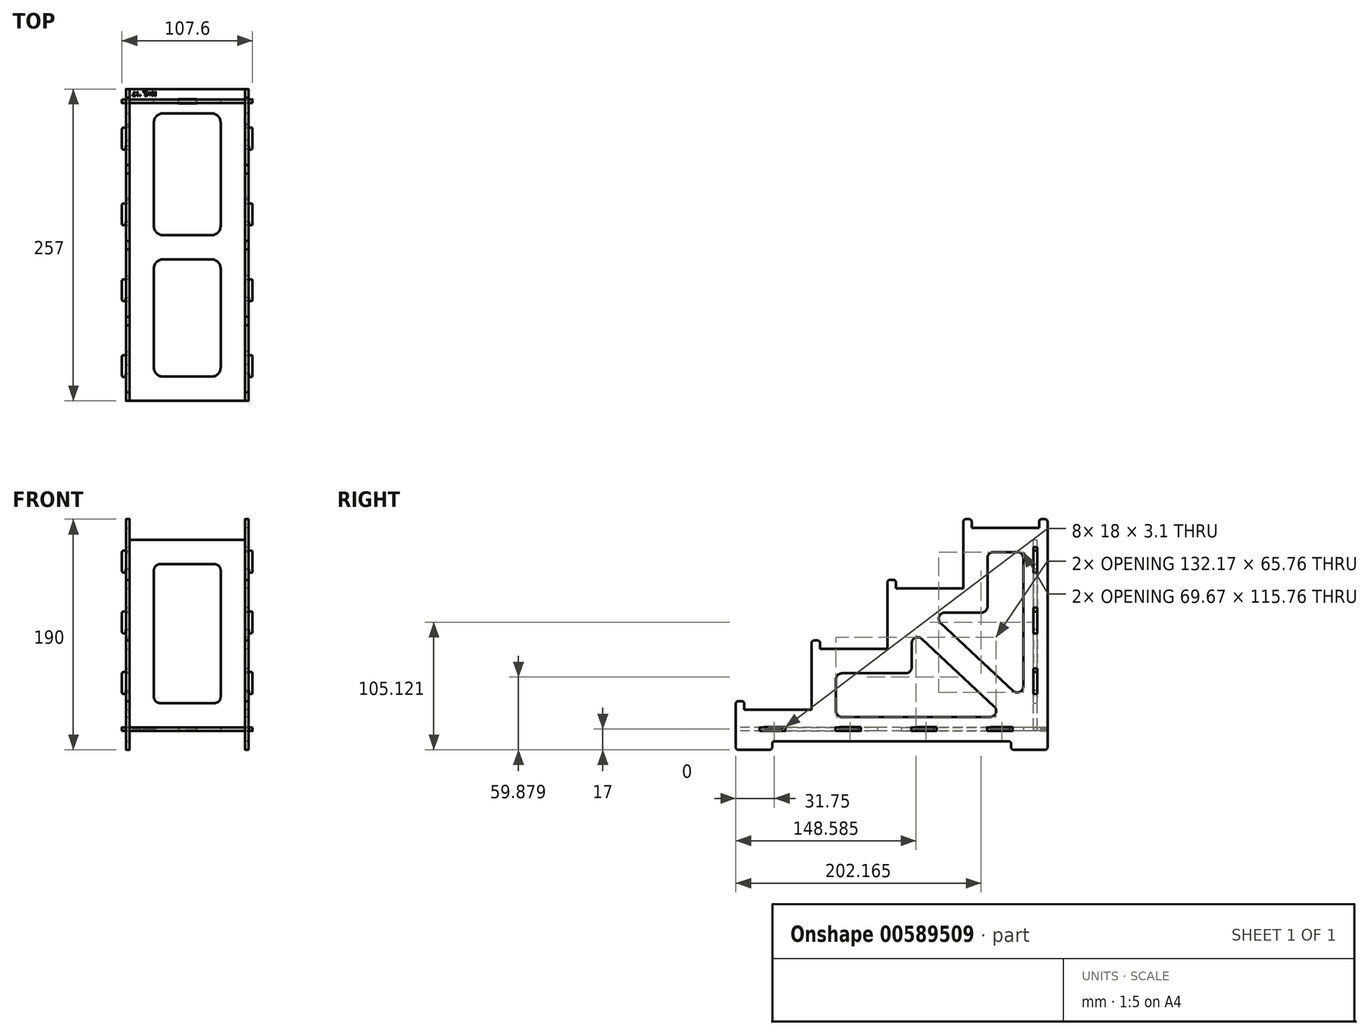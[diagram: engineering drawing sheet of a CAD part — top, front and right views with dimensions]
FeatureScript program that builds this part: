
annotation { "Feature Type Name" : "Feature", "Feature Type Description" : "" }
export const myFeature = defineFeature(function(context is Context, id is Id, definition is map)
    precondition{}
    {
        {
            var Q0;
            Q0=qCreatedBy(makeId("Right.planeOp"),FACE);
            cPlane(context, id + "F0", {"entities" : qUnion([Q0]), "cplaneType" : CPlaneType.OFFSET, "offset" : 95 / 2 * mm, "width" : 150 * mm, "height" : 150 * mm});
        }
        {
            assignVariable(context, id + "F1", {"name" : "Dicke", "anyValue" : 3 * mm});
        }
        {
            var Q0;
            Q0=qCreatedBy(id+"F0.planeOp",FACE);
            var sketch = newSketch(context, id + "F2", { "sketchPlane" : qUnion([Q0])});
            skLineSegment(sketch, "E0", {"start": v(-128.5, 2) * mm, "end": v(-128.5, 38) * mm});
            skLineSegment(sketch, "E1", {"start": v(-126.5, 40) * mm, "end": v(-123.5, 40) * mm});
            skLineSegment(sketch, "E2", {"start": v(-121.5, 38) * mm, "end": v(-121.5, 33) * mm});
            skLineSegment(sketch, "E3", {"start": v(-121.5, 33) * mm, "end": v(-66, 33) * mm});
            skLineSegment(sketch, "E4", {"start": v(-66, 33) * mm, "end": v(-66, 88) * mm});
            skLineSegment(sketch, "E5", {"start": v(-64, 90) * mm, "end": v(-61, 90) * mm});
            skLineSegment(sketch, "E6", {"start": v(-59, 88) * mm, "end": v(-59, 83) * mm});
            skLineSegment(sketch, "E7", {"start": v(-59, 83) * mm, "end": v(-3.5, 83) * mm});
            skLineSegment(sketch, "E8", {"start": v(-3.5, 83) * mm, "end": v(-3.5, 138) * mm});
            skLineSegment(sketch, "E9", {"start": v(-1.5, 140) * mm, "end": v(1.5, 140) * mm});
            skLineSegment(sketch, "E10", {"start": v(3.5, 138) * mm, "end": v(3.5, 133) * mm});
            skLineSegment(sketch, "E11", {"start": v(3.5, 133) * mm, "end": v(59, 133) * mm});
            skLineSegment(sketch, "E12", {"start": v(59, 133) * mm, "end": v(59, 188) * mm});
            skLineSegment(sketch, "E13", {"start": v(61, 190) * mm, "end": v(64, 190) * mm});
            skLineSegment(sketch, "E14", {"start": v(66, 188) * mm, "end": v(66, 183) * mm});
            skLineSegment(sketch, "E15", {"start": v(66, 183) * mm, "end": v(121.5, 183) * mm});
            skLineSegment(sketch, "E16", {"start": v(121.5, 183) * mm, "end": v(121.5, 188) * mm});
            skLineSegment(sketch, "E17", {"start": v(123.5, 190) * mm, "end": v(126.5, 190) * mm});
            skLineSegment(sketch, "E18", {"start": v(128.5, 188) * mm, "end": v(128.5, 2) * mm});
            skLineSegment(sketch, "E19", {"start": v(-126.5, 0) * mm, "end": v(-100.5, 0) * mm});
            skLineSegment(sketch, "E20", {"start": v(-98.5, 2) * mm, "end": v(-98.5, 5) * mm});
            skLineSegment(sketch, "E21", {"start": v(-96.5, 7) * mm, "end": v(96.5, 7) * mm});
            skLineSegment(sketch, "E22", {"start": v(98.5, 5) * mm, "end": v(98.5, 2) * mm});
            skLineSegment(sketch, "E23", {"start": v(100.5, 0) * mm, "end": v(126.5, 0) * mm});
            skPoint(sketch, "E24.visualSharp", {"position": v(-128.5, 0) * mm});
            skArc(sketch, "E24.filletArc", {"start": v(-128.5, 2) * mm, "mid": v(-127.91, 0.59) * mm, "end": v(-126.5, 0) * mm});
            skPoint(sketch, "E25.visualSharp", {"position": v(-128.5, 40) * mm});
            skArc(sketch, "E25.filletArc", {"start": v(-126.5, 40) * mm, "mid": v(-127.91, 39.41) * mm, "end": v(-128.5, 38) * mm});
            skPoint(sketch, "E26.visualSharp", {"position": v(-121.5, 40) * mm});
            skArc(sketch, "E26.filletArc", {"start": v(-121.5, 38) * mm, "mid": v(-122.09, 39.41) * mm, "end": v(-123.5, 40) * mm});
            skPoint(sketch, "E27.visualSharp", {"position": v(-66, 90) * mm});
            skArc(sketch, "E27.filletArc", {"start": v(-64, 90) * mm, "mid": v(-65.41, 89.41) * mm, "end": v(-66, 88) * mm});
            skPoint(sketch, "E28.visualSharp", {"position": v(-59, 90) * mm});
            skArc(sketch, "E28.filletArc", {"start": v(-59, 88) * mm, "mid": v(-59.59, 89.41) * mm, "end": v(-61, 90) * mm});
            skPoint(sketch, "E29.visualSharp", {"position": v(-3.5, 140) * mm});
            skArc(sketch, "E29.filletArc", {"start": v(-1.5, 140) * mm, "mid": v(-2.91, 139.41) * mm, "end": v(-3.5, 138) * mm});
            skPoint(sketch, "E30.visualSharp", {"position": v(3.5, 140) * mm});
            skArc(sketch, "E30.filletArc", {"start": v(3.5, 138) * mm, "mid": v(2.91, 139.41) * mm, "end": v(1.5, 140) * mm});
            skPoint(sketch, "E31.visualSharp", {"position": v(59, 190) * mm});
            skArc(sketch, "E31.filletArc", {"start": v(61, 190) * mm, "mid": v(59.59, 189.41) * mm, "end": v(59, 188) * mm});
            skPoint(sketch, "E32.visualSharp", {"position": v(66, 190) * mm});
            skArc(sketch, "E32.filletArc", {"start": v(66, 188) * mm, "mid": v(65.41, 189.41) * mm, "end": v(64, 190) * mm});
            skPoint(sketch, "E33.visualSharp", {"position": v(121.5, 190) * mm});
            skArc(sketch, "E33.filletArc", {"start": v(123.5, 190) * mm, "mid": v(122.09, 189.41) * mm, "end": v(121.5, 188) * mm});
            skPoint(sketch, "E34.visualSharp", {"position": v(128.5, 190) * mm});
            skArc(sketch, "E34.filletArc", {"start": v(128.5, 188) * mm, "mid": v(127.91, 189.41) * mm, "end": v(126.5, 190) * mm});
            skPoint(sketch, "E35.visualSharp", {"position": v(128.5, 0) * mm});
            skArc(sketch, "E35.filletArc", {"start": v(126.5, 0) * mm, "mid": v(127.91, 0.59) * mm, "end": v(128.5, 2) * mm});
            skPoint(sketch, "E36.visualSharp", {"position": v(98.5, 0) * mm});
            skArc(sketch, "E36.filletArc", {"start": v(98.5, 2) * mm, "mid": v(99.09, 0.59) * mm, "end": v(100.5, 0) * mm});
            skPoint(sketch, "E37.visualSharp", {"position": v(98.5, 7) * mm});
            skArc(sketch, "E37.filletArc", {"start": v(98.5, 5) * mm, "mid": v(97.91, 6.41) * mm, "end": v(96.5, 7) * mm});
            skPoint(sketch, "E38.visualSharp", {"position": v(-98.5, 7) * mm});
            skArc(sketch, "E38.filletArc", {"start": v(-96.5, 7) * mm, "mid": v(-97.91, 6.41) * mm, "end": v(-98.5, 5) * mm});
            skPoint(sketch, "E39.visualSharp", {"position": v(-98.5, 0) * mm});
            skArc(sketch, "E39.filletArc", {"start": v(-100.5, 0) * mm, "mid": v(-99.09, 0.59) * mm, "end": v(-98.5, 2) * mm});
            skLineSegment(sketch, "E40.bottom", {"start": v(-87.75, 15.45) * mm, "end": v(-105.75, 15.45) * mm});
            skLineSegment(sketch, "E40.top", {"start": v(-87.75, 18.55) * mm, "end": v(-105.75, 18.55) * mm});
            skLineSegment(sketch, "E40.left", {"start": v(-87.75, 15.45) * mm, "end": v(-87.75, 18.55) * mm});
            skLineSegment(sketch, "E40.right", {"start": v(-105.75, 15.45) * mm, "end": v(-105.75, 18.55) * mm});
            skPoint(sketch, "E40.middle", {"position": v(-96.75, 17) * mm});
            skPoint(sketch, "E41", {"position": v(-93.75, 33) * mm});
            skPoint(sketch, "E42", {"position": v(-31.25, 83) * mm});
            skPoint(sketch, "E43", {"position": v(31.25, 133) * mm});
            skPoint(sketch, "E44", {"position": v(93.75, 183) * mm});
            skLineSegment(sketch, "E45.1.0.0", {"start": v(-43.25, 15.45) * mm, "end": v(-43.25, 18.55) * mm});
            skLineSegment(sketch, "E45.1.0.1", {"start": v(-25.25, 15.45) * mm, "end": v(-25.25, 18.55) * mm});
            skLineSegment(sketch, "E45.1.0.2", {"start": v(-25.25, 18.55) * mm, "end": v(-43.25, 18.55) * mm});
            skPoint(sketch, "E45.1.0.3", {"position": v(-34.25, 17) * mm});
            skLineSegment(sketch, "E45.1.0.4", {"start": v(-25.25, 15.45) * mm, "end": v(-43.25, 15.45) * mm});
            skLineSegment(sketch, "E45.2.0.0", {"start": v(19.25, 15.45) * mm, "end": v(19.25, 18.55) * mm});
            skLineSegment(sketch, "E45.2.0.1", {"start": v(37.25, 15.45) * mm, "end": v(37.25, 18.55) * mm});
            skLineSegment(sketch, "E45.2.0.2", {"start": v(37.25, 18.55) * mm, "end": v(19.25, 18.55) * mm});
            skPoint(sketch, "E45.2.0.3", {"position": v(28.25, 17) * mm});
            skLineSegment(sketch, "E45.2.0.4", {"start": v(37.25, 15.45) * mm, "end": v(19.25, 15.45) * mm});
            skLineSegment(sketch, "E45.3.0.0", {"start": v(81.75, 15.45) * mm, "end": v(81.75, 18.55) * mm});
            skLineSegment(sketch, "E45.3.0.1", {"start": v(99.75, 15.45) * mm, "end": v(99.75, 18.55) * mm});
            skLineSegment(sketch, "E45.3.0.2", {"start": v(99.75, 18.55) * mm, "end": v(81.75, 18.55) * mm});
            skPoint(sketch, "E45.3.0.3", {"position": v(90.75, 17) * mm});
            skLineSegment(sketch, "E45.3.0.4", {"start": v(99.75, 15.45) * mm, "end": v(81.75, 15.45) * mm});
            skLineSegment(sketch, "E45.direction1", {"start": v(-105.75, 15.45) * mm, "end": v(-43.25, 15.45) * mm, "construction": true});
            skLineSegment(sketch, "E46", {"start": v(-93.75, 33) * mm, "end": v(-93.75, 7) * mm, "construction": true});
            skPoint(sketch, "E47", {"position": v(0, 7) * mm});
            skLineSegment(sketch, "E48.bottom", {"start": v(120.15, 149) * mm, "end": v(116.85, 149) * mm});
            skLineSegment(sketch, "E48.top", {"start": v(120.15, 167) * mm, "end": v(116.85, 167) * mm});
            skLineSegment(sketch, "E48.left", {"start": v(120.15, 149) * mm, "end": v(120.15, 167) * mm});
            skLineSegment(sketch, "E48.right", {"start": v(116.85, 149) * mm, "end": v(116.85, 167) * mm});
            skPoint(sketch, "E48.middle", {"position": v(118.5, 158) * mm});
            skLineSegment(sketch, "E49.1.0.0", {"start": v(120.15, 117) * mm, "end": v(116.85, 117) * mm});
            skLineSegment(sketch, "E49.1.0.1", {"start": v(120.15, 99) * mm, "end": v(116.85, 99) * mm});
            skLineSegment(sketch, "E49.1.0.2", {"start": v(116.85, 99) * mm, "end": v(116.85, 117) * mm});
            skPoint(sketch, "E49.1.0.3", {"position": v(118.5, 108) * mm});
            skLineSegment(sketch, "E49.1.0.4", {"start": v(120.15, 99) * mm, "end": v(120.15, 117) * mm});
            skLineSegment(sketch, "E49.2.0.0", {"start": v(120.15, 67) * mm, "end": v(116.85, 67) * mm});
            skLineSegment(sketch, "E49.2.0.1", {"start": v(120.15, 49) * mm, "end": v(116.85, 49) * mm});
            skLineSegment(sketch, "E49.2.0.2", {"start": v(116.85, 49) * mm, "end": v(116.85, 67) * mm});
            skPoint(sketch, "E49.2.0.3", {"position": v(118.5, 58) * mm});
            skLineSegment(sketch, "E49.2.0.4", {"start": v(120.15, 49) * mm, "end": v(120.15, 67) * mm});
            skLineSegment(sketch, "E49.direction1", {"start": v(116.85, 149) * mm, "end": v(116.85, 99) * mm, "construction": true});
            skLineSegment(sketch, "E50", {"start": v(-46, 32) * mm, "end": v(-46, 58) * mm});
            skLineSegment(sketch, "E51", {"start": v(-41, 63) * mm, "end": v(11.5, 63) * mm});
            skLineSegment(sketch, "E52", {"start": v(16.5, 68) * mm, "end": v(16.5, 87.8) * mm});
            skLineSegment(sketch, "E53", {"start": v(43.81, 113) * mm, "end": v(74, 113) * mm});
            skLineSegment(sketch, "E54", {"start": v(79, 118) * mm, "end": v(79, 158) * mm});
            skLineSegment(sketch, "E55", {"start": v(84, 163) * mm, "end": v(103.5, 163) * mm});
            skLineSegment(sketch, "E56", {"start": v(108.5, 158) * mm, "end": v(108.5, 52.2) * mm});
            skLineSegment(sketch, "E57", {"start": v(81.19, 27) * mm, "end": v(-41, 27) * mm});
            skLineSegment(sketch, "E58", {"start": v(24.91, 91.45) * mm, "end": v(84.6, 35.65) * mm});
            skLineSegment(sketch, "E59", {"start": v(40.4, 104.35) * mm, "end": v(100.09, 48.55) * mm});
            skPoint(sketch, "E60.visualSharp", {"position": v(-46, 27) * mm});
            skArc(sketch, "E60.filletArc", {"start": v(-46, 32) * mm, "mid": v(-44.54, 28.46) * mm, "end": v(-41, 27) * mm});
            skPoint(sketch, "E61.visualSharp", {"position": v(-46, 63) * mm});
            skArc(sketch, "E61.filletArc", {"start": v(-41, 63) * mm, "mid": v(-44.54, 61.54) * mm, "end": v(-46, 58) * mm});
            skPoint(sketch, "E62.visualSharp", {"position": v(16.5, 63) * mm});
            skArc(sketch, "E62.filletArc", {"start": v(11.5, 63) * mm, "mid": v(15.04, 64.46) * mm, "end": v(16.5, 68) * mm});
            skPoint(sketch, "E63.visualSharp", {"position": v(16.5, 99.31) * mm});
            skArc(sketch, "E63.filletArc", {"start": v(24.91, 91.45) * mm, "mid": v(19.5, 92.38) * mm, "end": v(16.5, 87.8) * mm});
            skPoint(sketch, "E64.visualSharp", {"position": v(93.86, 27) * mm});
            skArc(sketch, "E64.filletArc", {"start": v(81.19, 27) * mm, "mid": v(85.84, 30.16) * mm, "end": v(84.6, 35.65) * mm});
            skPoint(sketch, "E65.visualSharp", {"position": v(31.14, 113) * mm});
            skArc(sketch, "E65.filletArc", {"start": v(43.81, 113) * mm, "mid": v(39.16, 109.84) * mm, "end": v(40.4, 104.35) * mm});
            skPoint(sketch, "E66.visualSharp", {"position": v(108.5, 40.69) * mm});
            skArc(sketch, "E66.filletArc", {"start": v(100.09, 48.55) * mm, "mid": v(105.5, 47.62) * mm, "end": v(108.5, 52.2) * mm});
            skPoint(sketch, "E67.visualSharp", {"position": v(79, 113) * mm});
            skArc(sketch, "E67.filletArc", {"start": v(74, 113) * mm, "mid": v(77.54, 114.46) * mm, "end": v(79, 118) * mm});
            skPoint(sketch, "E68.visualSharp", {"position": v(108.5, 163) * mm});
            skArc(sketch, "E68.filletArc", {"start": v(108.5, 158) * mm, "mid": v(107.04, 161.54) * mm, "end": v(103.5, 163) * mm});
            skPoint(sketch, "E69.visualSharp", {"position": v(79, 163) * mm});
            skArc(sketch, "E69.filletArc", {"start": v(84, 163) * mm, "mid": v(80.46, 161.54) * mm, "end": v(79, 158) * mm});
            skSolve(sketch);
        }
        {
            var Q0;
            Q0=makeQuery(id+"F2.imprint","IMPRINT",FACE,{"disambiguationData":[TD([[makeQuery(id+"F2.imprint","IMPRINT",EDGE,{"derivedFrom":sQuery(id+"F2.wireOp",EDGE,"E0")}),-1.0]])]});
            extrude(context, id + "F3", {"entities" : qUnion([Q0]), "depth" : getVariable(context, 'Dicke'), "offsetDistance" : 25 * mm});
        }
        {
            var Q0;
            Q0=makeQuery(id+"F3.opExtrude","SWEPT_BODY",BODY,{"disambiguationData":[OSD([sQuery(id+"F2.wireOp",EDGE,"E0"),sQuery(id+"F2.wireOp",EDGE,"E1"),sQuery(id+"F2.wireOp",EDGE,"E2"),sQuery(id+"F2.wireOp",EDGE,"E3"),sQuery(id+"F2.wireOp",EDGE,"E4"),sQuery(id+"F2.wireOp",EDGE,"E5"),sQuery(id+"F2.wireOp",EDGE,"E6"),sQuery(id+"F2.wireOp",EDGE,"E7"),sQuery(id+"F2.wireOp",EDGE,"E8"),sQuery(id+"F2.wireOp",EDGE,"E9"),sQuery(id+"F2.wireOp",EDGE,"E10"),sQuery(id+"F2.wireOp",EDGE,"E11"),sQuery(id+"F2.wireOp",EDGE,"E12"),sQuery(id+"F2.wireOp",EDGE,"E13"),sQuery(id+"F2.wireOp",EDGE,"E14"),sQuery(id+"F2.wireOp",EDGE,"E15"),sQuery(id+"F2.wireOp",EDGE,"E16"),sQuery(id+"F2.wireOp",EDGE,"E17"),sQuery(id+"F2.wireOp",EDGE,"E18"),sQuery(id+"F2.wireOp",EDGE,"E19"),sQuery(id+"F2.wireOp",EDGE,"E20"),sQuery(id+"F2.wireOp",EDGE,"E21"),sQuery(id+"F2.wireOp",EDGE,"E22"),sQuery(id+"F2.wireOp",EDGE,"E23"),sQuery(id+"F2.wireOp",EDGE,"E24.filletArc"),sQuery(id+"F2.wireOp",EDGE,"E25.filletArc"),sQuery(id+"F2.wireOp",EDGE,"E26.filletArc"),sQuery(id+"F2.wireOp",EDGE,"E27.filletArc"),sQuery(id+"F2.wireOp",EDGE,"E28.filletArc"),sQuery(id+"F2.wireOp",EDGE,"E29.filletArc"),sQuery(id+"F2.wireOp",EDGE,"E30.filletArc"),sQuery(id+"F2.wireOp",EDGE,"E31.filletArc"),sQuery(id+"F2.wireOp",EDGE,"E32.filletArc"),sQuery(id+"F2.wireOp",EDGE,"E33.filletArc"),sQuery(id+"F2.wireOp",EDGE,"E34.filletArc"),sQuery(id+"F2.wireOp",EDGE,"E35.filletArc"),sQuery(id+"F2.wireOp",EDGE,"E36.filletArc"),sQuery(id+"F2.wireOp",EDGE,"E37.filletArc"),sQuery(id+"F2.wireOp",EDGE,"E38.filletArc"),sQuery(id+"F2.wireOp",EDGE,"E39.filletArc")])]});
            var Q1;
            Q1=qCreatedBy(makeId("Right.planeOp"),FACE);
            mirror(context, id + "F4", {"entities" : qUnion([Q0]), "mirrorPlane" : qUnion([Q1])});
        }
        {
            var Q0;
            Q0=qCreatedBy(makeId("Top.planeOp"),FACE);
            var Q1;
            Q1=sQuery(id+"F2.wireOp",VERTEX,"E45.2.0.3");
            cPlane(context, id + "F5", {"entities" : qUnion([Q0, Q1]), "cplaneType" : CPlaneType.PLANE_POINT, "offset" : 25 * mm, "width" : 150 * mm, "height" : 150 * mm});
        }
        {
            var Q0;
            Q0=qCreatedBy(id+"F5.planeOp",FACE);
            var sketch = newSketch(context, id + "F6", { "sketchPlane" : qUnion([Q0])});
            skLineSegment(sketch, "E70", {"start": v(0, 128.5) * mm, "end": v(47.5, 128.5) * mm});
            skLineSegment(sketch, "E71", {"start": v(47.5, 128.5) * mm, "end": v(47.5, 96.75) * mm});
            skLineSegment(sketch, "E72", {"start": v(47.5, 96.75) * mm, "end": v(52.8, 96.75) * mm});
            skLineSegment(sketch, "E73", {"start": v(53.8, 95.75) * mm, "end": v(53.8, 79.75) * mm});
            skLineSegment(sketch, "E74", {"start": v(52.8, 78.75) * mm, "end": v(50.8, 78.75) * mm});
            skLineSegment(sketch, "E75", {"start": v(50.8, 78.75) * mm, "end": v(50.8, 81.75) * mm});
            skLineSegment(sketch, "E76", {"start": v(50.8, 81.75) * mm, "end": v(47.5, 81.75) * mm});
            skLineSegment(sketch, "E77", {"start": v(47.5, 81.75) * mm, "end": v(47.5, 34.25) * mm});
            skLineSegment(sketch, "E78", {"start": v(47.5, 34.25) * mm, "end": v(52.8, 34.25) * mm});
            skLineSegment(sketch, "E79", {"start": v(53.8, 33.25) * mm, "end": v(53.8, 17.25) * mm});
            skLineSegment(sketch, "E80", {"start": v(52.8, 16.25) * mm, "end": v(50.8, 16.25) * mm});
            skLineSegment(sketch, "E81", {"start": v(50.8, 16.25) * mm, "end": v(50.8, 19.25) * mm});
            skLineSegment(sketch, "E82", {"start": v(50.8, 19.25) * mm, "end": v(47.5, 19.25) * mm});
            skLineSegment(sketch, "E83", {"start": v(47.5, 19.25) * mm, "end": v(47.5, -28.25) * mm});
            skLineSegment(sketch, "E84", {"start": v(47.5, -28.25) * mm, "end": v(52.8, -28.25) * mm});
            skLineSegment(sketch, "E85", {"start": v(53.8, -29.25) * mm, "end": v(53.8, -45.25) * mm});
            skLineSegment(sketch, "E86", {"start": v(52.8, -46.25) * mm, "end": v(50.8, -46.25) * mm});
            skLineSegment(sketch, "E87", {"start": v(50.8, -46.25) * mm, "end": v(50.8, -43.25) * mm});
            skLineSegment(sketch, "E88", {"start": v(50.8, -43.25) * mm, "end": v(47.5, -43.25) * mm});
            skLineSegment(sketch, "E89", {"start": v(47.5, -43.25) * mm, "end": v(47.5, -90.75) * mm});
            skLineSegment(sketch, "E90", {"start": v(50.8, -105.75) * mm, "end": v(47.5, -105.75) * mm});
            skLineSegment(sketch, "E91", {"start": v(47.5, -105.75) * mm, "end": v(47.5, -128.5) * mm});
            skLineSegment(sketch, "E92", {"start": v(47.5, -128.5) * mm, "end": v(0, -128.5) * mm});
            skLineSegment(sketch, "E93", {"start": v(47.5, -90.75) * mm, "end": v(52.8, -90.75) * mm});
            skLineSegment(sketch, "E94", {"start": v(53.8, -91.75) * mm, "end": v(53.8, -107.75) * mm});
            skLineSegment(sketch, "E95", {"start": v(52.8, -108.75) * mm, "end": v(50.8, -108.75) * mm});
            skLineSegment(sketch, "E96", {"start": v(50.8, -108.75) * mm, "end": v(50.8, -105.75) * mm});
            skPoint(sketch, "E97.visualSharp", {"position": v(53.8, 96.75) * mm});
            skArc(sketch, "E97.filletArc", {"start": v(53.8, 95.75) * mm, "mid": v(53.5, 96.46) * mm, "end": v(52.8, 96.75) * mm});
            skPoint(sketch, "E98.visualSharp", {"position": v(53.8, 78.75) * mm});
            skArc(sketch, "E98.filletArc", {"start": v(52.8, 78.75) * mm, "mid": v(53.5, 79.04) * mm, "end": v(53.8, 79.75) * mm});
            skPoint(sketch, "E99.visualSharp", {"position": v(53.8, 34.25) * mm});
            skArc(sketch, "E99.filletArc", {"start": v(53.8, 33.25) * mm, "mid": v(53.5, 33.96) * mm, "end": v(52.8, 34.25) * mm});
            skPoint(sketch, "E100.visualSharp", {"position": v(53.8, 16.25) * mm});
            skArc(sketch, "E100.filletArc", {"start": v(52.8, 16.25) * mm, "mid": v(53.5, 16.54) * mm, "end": v(53.8, 17.25) * mm});
            skPoint(sketch, "E101.visualSharp", {"position": v(53.8, -28.25) * mm});
            skArc(sketch, "E101.filletArc", {"start": v(53.8, -29.25) * mm, "mid": v(53.5, -28.54) * mm, "end": v(52.8, -28.25) * mm});
            skPoint(sketch, "E102.visualSharp", {"position": v(53.8, -46.25) * mm});
            skArc(sketch, "E102.filletArc", {"start": v(52.8, -46.25) * mm, "mid": v(53.5, -45.96) * mm, "end": v(53.8, -45.25) * mm});
            skPoint(sketch, "E103.visualSharp", {"position": v(53.8, -90.75) * mm});
            skArc(sketch, "E103.filletArc", {"start": v(53.8, -91.75) * mm, "mid": v(53.5, -91.04) * mm, "end": v(52.8, -90.75) * mm});
            skPoint(sketch, "E104.visualSharp", {"position": v(53.8, -108.75) * mm});
            skArc(sketch, "E104.filletArc", {"start": v(52.8, -108.75) * mm, "mid": v(53.5, -108.46) * mm, "end": v(53.8, -107.75) * mm});
            skLineSegment(sketch, "E105.MirrorCS", {"start": v(-52.8, -108.75) * mm, "end": v(-50.8, -108.75) * mm});
            skArc(sketch, "E106.MirrorCS", {"start": v(-53.8, -29.25) * mm, "mid": v(-53.5, -28.54) * mm, "end": v(-52.8, -28.25) * mm});
            skLineSegment(sketch, "E107.MirrorCS", {"start": v(-50.8, -108.75) * mm, "end": v(-50.8, -105.75) * mm});
            skArc(sketch, "E108.MirrorCS", {"start": v(-52.8, -108.75) * mm, "mid": v(-53.5, -108.46) * mm, "end": v(-53.8, -107.75) * mm});
            skLineSegment(sketch, "E109.MirrorCS", {"start": v(-50.8, 78.75) * mm, "end": v(-50.8, 81.75) * mm});
            skLineSegment(sketch, "E110.MirrorCS", {"start": v(-52.8, 78.75) * mm, "end": v(-50.8, 78.75) * mm});
            skArc(sketch, "E111.MirrorCS", {"start": v(-53.8, 33.25) * mm, "mid": v(-53.5, 33.96) * mm, "end": v(-52.8, 34.25) * mm});
            skArc(sketch, "E112.MirrorCS", {"start": v(-53.8, -91.75) * mm, "mid": v(-53.5, -91.04) * mm, "end": v(-52.8, -90.75) * mm});
            skArc(sketch, "E113.MirrorCS", {"start": v(-52.8, 16.25) * mm, "mid": v(-53.5, 16.54) * mm, "end": v(-53.8, 17.25) * mm});
            skArc(sketch, "E114.MirrorCS", {"start": v(-53.8, 95.75) * mm, "mid": v(-53.5, 96.46) * mm, "end": v(-52.8, 96.75) * mm});
            skArc(sketch, "E115.MirrorCS", {"start": v(-52.8, 78.75) * mm, "mid": v(-53.5, 79.04) * mm, "end": v(-53.8, 79.75) * mm});
            skArc(sketch, "E116.MirrorCS", {"start": v(-52.8, -46.25) * mm, "mid": v(-53.5, -45.96) * mm, "end": v(-53.8, -45.25) * mm});
            skLineSegment(sketch, "E117.MirrorCS", {"start": v(-52.8, -46.25) * mm, "end": v(-50.8, -46.25) * mm});
            skLineSegment(sketch, "E118.MirrorCS", {"start": v(-50.8, -46.25) * mm, "end": v(-50.8, -43.25) * mm});
            skLineSegment(sketch, "E119.MirrorCS", {"start": v(-50.8, 81.75) * mm, "end": v(-47.5, 81.75) * mm});
            skLineSegment(sketch, "E120.MirrorCS", {"start": v(-50.8, 16.25) * mm, "end": v(-50.8, 19.25) * mm});
            skLineSegment(sketch, "E121.MirrorCS", {"start": v(-52.8, 16.25) * mm, "end": v(-50.8, 16.25) * mm});
            skLineSegment(sketch, "E122.MirrorCS", {"start": v(-47.5, -28.25) * mm, "end": v(-52.8, -28.25) * mm});
            skLineSegment(sketch, "E123.MirrorCS", {"start": v(-47.5, 96.75) * mm, "end": v(-52.8, 96.75) * mm});
            skLineSegment(sketch, "E124.MirrorCS", {"start": v(-50.8, -105.75) * mm, "end": v(-47.5, -105.75) * mm});
            skLineSegment(sketch, "E125.MirrorCS", {"start": v(-50.8, -43.25) * mm, "end": v(-47.5, -43.25) * mm});
            skLineSegment(sketch, "E126.MirrorCS", {"start": v(-47.5, 34.25) * mm, "end": v(-52.8, 34.25) * mm});
            skLineSegment(sketch, "E127.MirrorCS", {"start": v(-50.8, 19.25) * mm, "end": v(-47.5, 19.25) * mm});
            skLineSegment(sketch, "E128.MirrorCS", {"start": v(-47.5, -90.75) * mm, "end": v(-52.8, -90.75) * mm});
            skLineSegment(sketch, "E129.MirrorCS", {"start": v(-47.5, 19.25) * mm, "end": v(-47.5, -28.25) * mm});
            skPoint(sketch, "E130.MirrorP", {"position": v(-53.8, 16.25) * mm});
            skLineSegment(sketch, "E131.MirrorCS", {"start": v(-53.8, 33.25) * mm, "end": v(-53.8, 17.25) * mm});
            skLineSegment(sketch, "E132.MirrorCS", {"start": v(-47.5, -105.75) * mm, "end": v(-47.5, -128.5) * mm});
            skPoint(sketch, "E133.MirrorP", {"position": v(-53.8, -46.25) * mm});
            skPoint(sketch, "E134.MirrorP", {"position": v(-53.8, 96.75) * mm});
            skLineSegment(sketch, "E135.MirrorCS", {"start": v(0, 128.5) * mm, "end": v(-47.5, 128.5) * mm});
            skPoint(sketch, "E136.MirrorP", {"position": v(-53.8, -108.75) * mm});
            skLineSegment(sketch, "E137.MirrorCS", {"start": v(-47.5, 81.75) * mm, "end": v(-47.5, 34.25) * mm});
            skLineSegment(sketch, "E138.MirrorCS", {"start": v(-47.5, 128.5) * mm, "end": v(-47.5, 96.75) * mm});
            skPoint(sketch, "E139.MirrorP", {"position": v(-53.8, 34.25) * mm});
            skPoint(sketch, "E140.MirrorP", {"position": v(-53.8, -28.25) * mm});
            skLineSegment(sketch, "E141.MirrorCS", {"start": v(-53.8, 95.75) * mm, "end": v(-53.8, 79.75) * mm});
            skLineSegment(sketch, "E142.MirrorCS", {"start": v(-53.8, -91.75) * mm, "end": v(-53.8, -107.75) * mm});
            skPoint(sketch, "E143.MirrorP", {"position": v(-53.8, 78.75) * mm});
            skLineSegment(sketch, "E144.MirrorCS", {"start": v(-53.8, -29.25) * mm, "end": v(-53.8, -45.25) * mm});
            skPoint(sketch, "E145.MirrorP", {"position": v(-53.8, -90.75) * mm});
            skLineSegment(sketch, "E146.MirrorCS", {"start": v(-47.5, -128.5) * mm, "end": v(0, -128.5) * mm});
            skLineSegment(sketch, "E147.MirrorCS", {"start": v(-47.5, -43.25) * mm, "end": v(-47.5, -90.75) * mm});
            skLineSegment(sketch, "E148.bottom", {"start": v(7.5, 120.15) * mm, "end": v(-7.5, 120.15) * mm});
            skLineSegment(sketch, "E148.top", {"start": v(7.5, 116.85) * mm, "end": v(-7.5, 116.85) * mm});
            skLineSegment(sketch, "E148.left", {"start": v(7.5, 120.15) * mm, "end": v(7.5, 116.85) * mm});
            skLineSegment(sketch, "E148.right", {"start": v(-7.5, 120.15) * mm, "end": v(-7.5, 116.85) * mm});
            skPoint(sketch, "E148.middle", {"position": v(0, 118.5) * mm});
            skPoint(sketch, "E149.endSnap0", {"position": v(-47.5, -4.5) * mm});
            skLineSegment(sketch, "E150.bottom", {"start": v(-20, 8.13) * mm, "end": v(20, 8.13) * mm});
            skLineSegment(sketch, "E150.top", {"start": v(-20, 108.5) * mm, "end": v(20, 108.5) * mm});
            skLineSegment(sketch, "E150.left", {"start": v(-27.5, 15.63) * mm, "end": v(-27.5, 101) * mm});
            skLineSegment(sketch, "E150.right", {"start": v(27.5, 15.63) * mm, "end": v(27.5, 101) * mm});
            skPoint(sketch, "E150.middle", {"position": v(0, 58.32) * mm});
            skLineSegment(sketch, "E151.bottom", {"start": v(-20, -108.5) * mm, "end": v(20, -108.5) * mm});
            skLineSegment(sketch, "E151.top", {"start": v(-20, -11.87) * mm, "end": v(20, -11.87) * mm});
            skLineSegment(sketch, "E151.left", {"start": v(-27.5, -101) * mm, "end": v(-27.5, -19.37) * mm});
            skLineSegment(sketch, "E151.right", {"start": v(27.5, -101) * mm, "end": v(27.5, -19.37) * mm});
            skPoint(sketch, "E151.middle", {"position": v(0, -60.18) * mm});
            skPoint(sketch, "E152.visualSharp", {"position": v(27.5, 108.5) * mm});
            skArc(sketch, "E152.filletArc", {"start": v(27.5, 101) * mm, "mid": v(25.3, 106.3) * mm, "end": v(20, 108.5) * mm});
            skPoint(sketch, "E153.visualSharp", {"position": v(-27.5, 108.5) * mm});
            skArc(sketch, "E153.filletArc", {"start": v(-20, 108.5) * mm, "mid": v(-25.3, 106.3) * mm, "end": v(-27.5, 101) * mm});
            skPoint(sketch, "E154.visualSharp", {"position": v(-27.5, 8.13) * mm});
            skArc(sketch, "E154.filletArc", {"start": v(-27.5, 15.63) * mm, "mid": v(-25.3, 10.33) * mm, "end": v(-20, 8.13) * mm});
            skPoint(sketch, "E155.visualSharp", {"position": v(27.5, 8.13) * mm});
            skArc(sketch, "E155.filletArc", {"start": v(20, 8.13) * mm, "mid": v(25.3, 10.33) * mm, "end": v(27.5, 15.63) * mm});
            skPoint(sketch, "E156.visualSharp", {"position": v(27.5, -11.87) * mm});
            skArc(sketch, "E156.filletArc", {"start": v(27.5, -19.37) * mm, "mid": v(25.3, -14.06) * mm, "end": v(20, -11.87) * mm});
            skPoint(sketch, "E157.visualSharp", {"position": v(-27.5, -11.87) * mm});
            skArc(sketch, "E157.filletArc", {"start": v(-20, -11.87) * mm, "mid": v(-25.3, -14.06) * mm, "end": v(-27.5, -19.37) * mm});
            skPoint(sketch, "E158.visualSharp", {"position": v(-27.5, -108.5) * mm});
            skArc(sketch, "E158.filletArc", {"start": v(-27.5, -101) * mm, "mid": v(-25.3, -106.3) * mm, "end": v(-20, -108.5) * mm});
            skPoint(sketch, "E159.visualSharp", {"position": v(27.5, -108.5) * mm});
            skArc(sketch, "E159.filletArc", {"start": v(20, -108.5) * mm, "mid": v(25.3, -106.3) * mm, "end": v(27.5, -101) * mm});
            skText(sketch, "E160", { "text": "N+S, \'17", "fontName": "OpenSans-Regular.ttf"});
            const initialGuessF6  = {"E160": [-0.02555, 0.1265, -1, 0, 0.00382]};
            skSetInitialGuess(sketch, initialGuessF6);
            skSolve(sketch);
        }
        {
            var Q0;
            Q0=makeQuery(id+"F6.imprint","IMPRINT",FACE,{"disambiguationData":[TD([[makeQuery(id+"F6.imprint","IMPRINT",EDGE,{"derivedFrom":sQuery(id+"F6.wireOp",EDGE,"E70")}),-1.0]])]});
            extrude(context, id + "F7", {"entities" : qUnion([Q0]), "endBound" : BoundingType.SYMMETRIC, "depth" : 3 * mm, "offsetDistance" : 25 * mm});
        }
        {
            var Q0;
            Q0=qCreatedBy(makeId("Front.planeOp"),FACE);
            var Q1;
            Q1=sQuery(id+"F6.wireOp",VERTEX,"E148.middle");
            cPlane(context, id + "F8", {"entities" : qUnion([Q0, Q1]), "cplaneType" : CPlaneType.PLANE_POINT, "offset" : 25 * mm, "width" : 150 * mm, "height" : 150 * mm});
        }
        {
            var Q0;
            Q0=qCreatedBy(id+"F8.planeOp",FACE);
            var sketch = newSketch(context, id + "F9", { "sketchPlane" : qUnion([Q0])});
            skLineSegment(sketch, "E161", {"start": v(0, 16.01) * mm, "end": v(6.25, 16.01) * mm});
            skLineSegment(sketch, "E162", {"start": v(7.24, 16.91) * mm, "end": v(7.4, 18.5) * mm});
            skLineSegment(sketch, "E163", {"start": v(7.4, 18.5) * mm, "end": v(47.5, 18.5) * mm});
            skLineSegment(sketch, "E164", {"start": v(47.5, 18.5) * mm, "end": v(47.5, 49) * mm});
            skLineSegment(sketch, "E165", {"start": v(47.5, 49) * mm, "end": v(50.8, 49) * mm});
            skLineSegment(sketch, "E166", {"start": v(50.8, 49) * mm, "end": v(50.8, 46) * mm});
            skLineSegment(sketch, "E167", {"start": v(50.8, 46) * mm, "end": v(52.8, 46) * mm});
            skLineSegment(sketch, "E168", {"start": v(53.8, 47) * mm, "end": v(53.8, 63) * mm});
            skLineSegment(sketch, "E169", {"start": v(52.8, 64) * mm, "end": v(47.5, 64) * mm});
            skLineSegment(sketch, "E170", {"start": v(47.5, 64) * mm, "end": v(47.5, 99) * mm});
            skLineSegment(sketch, "E171", {"start": v(47.5, 99) * mm, "end": v(50.8, 99) * mm});
            skLineSegment(sketch, "E172", {"start": v(50.8, 99) * mm, "end": v(50.8, 96) * mm});
            skLineSegment(sketch, "E173", {"start": v(50.8, 96) * mm, "end": v(52.8, 96) * mm});
            skLineSegment(sketch, "E174", {"start": v(53.8, 97) * mm, "end": v(53.8, 113) * mm});
            skLineSegment(sketch, "E175", {"start": v(52.8, 114) * mm, "end": v(47.5, 114) * mm});
            skLineSegment(sketch, "E176", {"start": v(47.5, 114) * mm, "end": v(47.5, 149) * mm});
            skLineSegment(sketch, "E177", {"start": v(47.5, 149) * mm, "end": v(50.8, 149) * mm});
            skLineSegment(sketch, "E178", {"start": v(50.8, 149) * mm, "end": v(50.8, 146) * mm});
            skLineSegment(sketch, "E179", {"start": v(50.8, 146) * mm, "end": v(52.8, 146) * mm});
            skLineSegment(sketch, "E180", {"start": v(53.8, 147) * mm, "end": v(53.8, 163) * mm});
            skLineSegment(sketch, "E181", {"start": v(52.8, 164) * mm, "end": v(47.5, 164) * mm});
            skLineSegment(sketch, "E182", {"start": v(47.5, 164) * mm, "end": v(47.5, 173) * mm});
            skPoint(sketch, "E183.visualSharp", {"position": v(7.15, 16.01) * mm});
            skArc(sketch, "E183.filletArc", {"start": v(6.25, 16.01) * mm, "mid": v(6.92, 16.27) * mm, "end": v(7.24, 16.91) * mm});
            skPoint(sketch, "E184.visualSharp", {"position": v(53.8, 46) * mm});
            skArc(sketch, "E184.filletArc", {"start": v(52.8, 46) * mm, "mid": v(53.5, 46.3) * mm, "end": v(53.8, 47) * mm});
            skPoint(sketch, "E185.visualSharp", {"position": v(53.8, 64) * mm});
            skArc(sketch, "E185.filletArc", {"start": v(53.8, 63) * mm, "mid": v(53.5, 63.7) * mm, "end": v(52.8, 64) * mm});
            skPoint(sketch, "E186.visualSharp", {"position": v(53.8, 96) * mm});
            skArc(sketch, "E186.filletArc", {"start": v(52.8, 96) * mm, "mid": v(53.5, 96.3) * mm, "end": v(53.8, 97) * mm});
            skPoint(sketch, "E187.visualSharp", {"position": v(53.8, 114) * mm});
            skArc(sketch, "E187.filletArc", {"start": v(53.8, 113) * mm, "mid": v(53.5, 113.7) * mm, "end": v(52.8, 114) * mm});
            skPoint(sketch, "E188.visualSharp", {"position": v(53.8, 146) * mm});
            skArc(sketch, "E188.filletArc", {"start": v(52.8, 146) * mm, "mid": v(53.5, 146.3) * mm, "end": v(53.8, 147) * mm});
            skPoint(sketch, "E189.visualSharp", {"position": v(53.8, 164) * mm});
            skArc(sketch, "E189.filletArc", {"start": v(53.8, 163) * mm, "mid": v(53.5, 163.7) * mm, "end": v(52.8, 164) * mm});
            skArc(sketch, "E190.MirrorCS", {"start": v(-6.25, 16.01) * mm, "mid": v(-6.92, 16.27) * mm, "end": v(-7.24, 16.91) * mm});
            skLineSegment(sketch, "E191.MirrorCS", {"start": v(-50.8, 149) * mm, "end": v(-50.8, 146) * mm});
            skLineSegment(sketch, "E192.MirrorCS", {"start": v(-50.8, 96) * mm, "end": v(-52.8, 96) * mm});
            skLineSegment(sketch, "E193.MirrorCS", {"start": v(-50.8, 49) * mm, "end": v(-50.8, 46) * mm});
            skLineSegment(sketch, "E194.MirrorCS", {"start": v(-50.8, 146) * mm, "end": v(-52.8, 146) * mm});
            skLineSegment(sketch, "E195.MirrorCS", {"start": v(-50.8, 99) * mm, "end": v(-50.8, 96) * mm});
            skArc(sketch, "E196.MirrorCS", {"start": v(-52.8, 96) * mm, "mid": v(-53.5, 96.3) * mm, "end": v(-53.8, 97) * mm});
            skArc(sketch, "E197.MirrorCS", {"start": v(-52.8, 46) * mm, "mid": v(-53.5, 46.3) * mm, "end": v(-53.8, 47) * mm});
            skArc(sketch, "E198.MirrorCS", {"start": v(-52.8, 146) * mm, "mid": v(-53.5, 146.3) * mm, "end": v(-53.8, 147) * mm});
            skLineSegment(sketch, "E199.MirrorCS", {"start": v(-50.8, 46) * mm, "end": v(-52.8, 46) * mm});
            skArc(sketch, "E200.MirrorCS", {"start": v(-53.8, 163) * mm, "mid": v(-53.5, 163.7) * mm, "end": v(-52.8, 164) * mm});
            skArc(sketch, "E201.MirrorCS", {"start": v(-53.8, 113) * mm, "mid": v(-53.5, 113.7) * mm, "end": v(-52.8, 114) * mm});
            skArc(sketch, "E202.MirrorCS", {"start": v(-53.8, 63) * mm, "mid": v(-53.5, 63.7) * mm, "end": v(-52.8, 64) * mm});
            skLineSegment(sketch, "E203.MirrorCS", {"start": v(-52.8, 164) * mm, "end": v(-47.5, 164) * mm});
            skLineSegment(sketch, "E204.MirrorCS", {"start": v(-47.5, 49) * mm, "end": v(-50.8, 49) * mm});
            skLineSegment(sketch, "E205.MirrorCS", {"start": v(-47.5, 99) * mm, "end": v(-50.8, 99) * mm});
            skLineSegment(sketch, "E206.MirrorCS", {"start": v(-7.24, 16.91) * mm, "end": v(-7.4, 18.5) * mm});
            skLineSegment(sketch, "E207.MirrorCS", {"start": v(-52.8, 64) * mm, "end": v(-47.5, 64) * mm});
            skLineSegment(sketch, "E208.MirrorCS", {"start": v(-47.5, 149) * mm, "end": v(-50.8, 149) * mm});
            skLineSegment(sketch, "E209.MirrorCS", {"start": v(-52.8, 114) * mm, "end": v(-47.5, 114) * mm});
            skLineSegment(sketch, "E210.MirrorCS", {"start": v(-47.5, 164) * mm, "end": v(-47.5, 173) * mm});
            skPoint(sketch, "E211.MirrorP", {"position": v(-7.15, 16.01) * mm});
            skLineSegment(sketch, "E212.MirrorCS", {"start": v(0, 16.01) * mm, "end": v(-6.25, 16.01) * mm});
            skPoint(sketch, "E213.MirrorP", {"position": v(-53.8, 114) * mm});
            skLineSegment(sketch, "E214.MirrorCS", {"start": v(-47.5, 114) * mm, "end": v(-47.5, 149) * mm});
            skLineSegment(sketch, "E215.MirrorCS", {"start": v(-53.8, 147) * mm, "end": v(-53.8, 163) * mm});
            skLineSegment(sketch, "E216.MirrorCS", {"start": v(-47.5, 64) * mm, "end": v(-47.5, 99) * mm});
            skLineSegment(sketch, "E217.MirrorCS", {"start": v(-53.8, 47) * mm, "end": v(-53.8, 63) * mm});
            skLineSegment(sketch, "E218.MirrorCS", {"start": v(-7.4, 18.5) * mm, "end": v(-47.5, 18.5) * mm});
            skLineSegment(sketch, "E219.MirrorCS", {"start": v(-47.5, 18.5) * mm, "end": v(-47.5, 49) * mm});
            skLineSegment(sketch, "E220.MirrorCS", {"start": v(-53.8, 97) * mm, "end": v(-53.8, 113) * mm});
            skPoint(sketch, "E221.MirrorP", {"position": v(-53.8, 96) * mm});
            skPoint(sketch, "E222.MirrorP", {"position": v(-53.8, 146) * mm});
            skPoint(sketch, "E223.MirrorP", {"position": v(-53.8, 164) * mm});
            skPoint(sketch, "E224.MirrorP", {"position": v(-53.8, 46) * mm});
            skPoint(sketch, "E225.MirrorP", {"position": v(-53.8, 64) * mm});
            skLineSegment(sketch, "E226", {"start": v(-47.5, 173) * mm, "end": v(47.5, 173) * mm});
            skLineSegment(sketch, "E227.bottom", {"start": v(22.5, 153) * mm, "end": v(-22.5, 153) * mm});
            skLineSegment(sketch, "E227.top", {"start": v(22.5, 38.5) * mm, "end": v(-22.5, 38.5) * mm});
            skLineSegment(sketch, "E227.left", {"start": v(27.5, 148) * mm, "end": v(27.5, 43.5) * mm});
            skLineSegment(sketch, "E227.right", {"start": v(-27.5, 148) * mm, "end": v(-27.5, 43.5) * mm});
            skPoint(sketch, "E227.middle", {"position": v(0, 95.75) * mm});
            skPoint(sketch, "E228.visualSharp", {"position": v(-27.5, 153) * mm});
            skArc(sketch, "E228.filletArc", {"start": v(-22.5, 153) * mm, "mid": v(-26.04, 151.54) * mm, "end": v(-27.5, 148) * mm});
            skPoint(sketch, "E229.visualSharp", {"position": v(27.5, 153) * mm});
            skArc(sketch, "E229.filletArc", {"start": v(27.5, 148) * mm, "mid": v(26.04, 151.54) * mm, "end": v(22.5, 153) * mm});
            skPoint(sketch, "E230.visualSharp", {"position": v(27.5, 38.5) * mm});
            skArc(sketch, "E230.filletArc", {"start": v(22.5, 38.5) * mm, "mid": v(26.04, 39.96) * mm, "end": v(27.5, 43.5) * mm});
            skPoint(sketch, "E231.visualSharp", {"position": v(-27.5, 38.5) * mm});
            skArc(sketch, "E231.filletArc", {"start": v(-27.5, 43.5) * mm, "mid": v(-26.04, 39.96) * mm, "end": v(-22.5, 38.5) * mm});
            skSolve(sketch);
        }
        {
            var Q0;
            Q0=makeQuery(id+"F9.imprint","IMPRINT",FACE,{"disambiguationData":[TD([[makeQuery(id+"F9.imprint","IMPRINT",EDGE,{"derivedFrom":sQuery(id+"F9.wireOp",EDGE,"E161")}),1.0]])]});
            extrude(context, id + "F10", {"entities" : qUnion([Q0]), "endBound" : BoundingType.SYMMETRIC, "depth" : 3 * mm, "offsetDistance" : 25 * mm});
        }
    });
